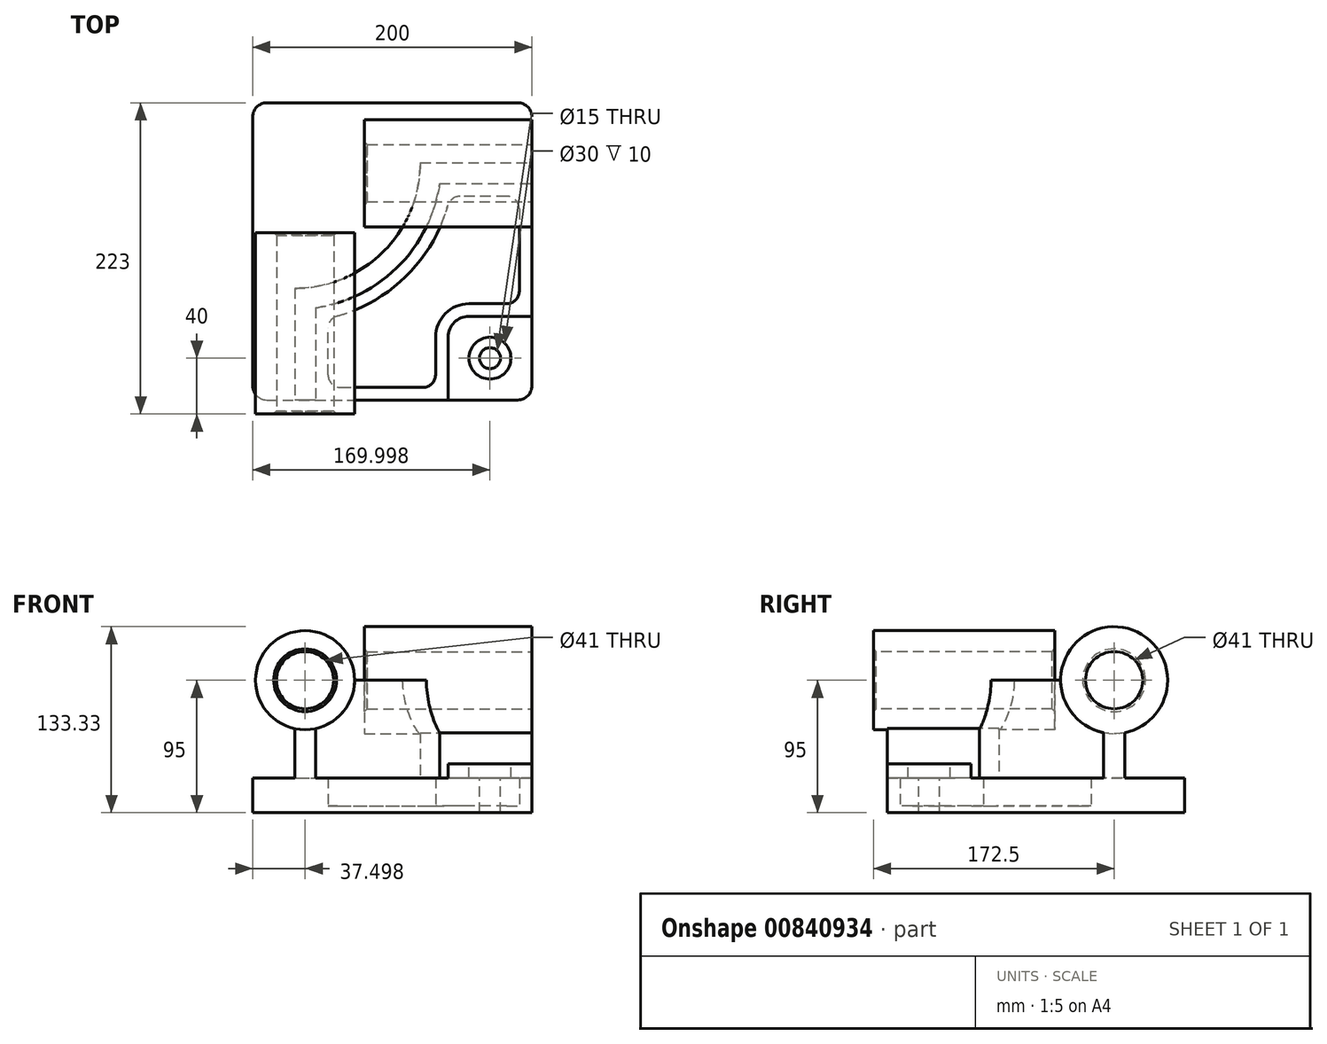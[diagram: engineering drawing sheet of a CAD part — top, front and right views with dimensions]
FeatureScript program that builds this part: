
annotation { "Feature Type Name" : "Feature", "Feature Type Description" : "" }
export const myFeature = defineFeature(function(context is Context, id is Id, definition is map)
    precondition{}
    {
        {
            assignVariable(context, id + "F0", {"name" : "D", "anyValue" : 130});
        }
        {
            var Q0;
            Q0=qCreatedBy(makeId("Top.planeOp"),FACE);
            var sketch = newSketch(context, id + "F1", { "sketchPlane" : qUnion([Q0])});
            skLineSegment(sketch, "E0.bottom", {"start": v(-118.1, 102.93) * mm, "end": v(61.9, 102.93) * mm});
            skLineSegment(sketch, "E0.top", {"start": v(-118.1, -110.07) * mm, "end": v(-83.1, -110.07) * mm});
            skLineSegment(sketch, "E0.left", {"start": v(-128.1, 92.93) * mm, "end": v(-128.1, -100.07) * mm});
            skLineSegment(sketch, "E0.right", {"start": v(71.9, 92.93) * mm, "end": v(71.9, 44.93) * mm});
            skCircle(sketch, "E1", {"center": v(41.9, -80.07) * mm, "radius": 11.73 * mm});
            skCircle(sketch, "E2", {"center": v(41.9, -80.07) * mm, "radius": 6.14 * mm});
            skPoint(sketch, "E3.visualSharp", {"position": v(-128.1, 102.93) * mm});
            skArc(sketch, "E3.filletArc", {"start": v(-118.1, 102.93) * mm, "mid": v(-125.16, 100) * mm, "end": v(-128.1, 92.93) * mm});
            skPoint(sketch, "E4.visualSharp", {"position": v(-128.1, -110.07) * mm});
            skArc(sketch, "E4.filletArc", {"start": v(-128.1, -100.07) * mm, "mid": v(-125.16, -107.14) * mm, "end": v(-118.1, -110.07) * mm});
            skPoint(sketch, "E5.visualSharp", {"position": v(71.9, -110.07) * mm});
            skArc(sketch, "E5.filletArc", {"start": v(61.9, -110.07) * mm, "mid": v(68.98, -107.14) * mm, "end": v(71.9, -100.07) * mm});
            skPoint(sketch, "E6.visualSharp", {"position": v(71.9, 102.93) * mm});
            skArc(sketch, "E6.filletArc", {"start": v(71.9, 92.93) * mm, "mid": v(68.98, 100) * mm, "end": v(61.9, 102.93) * mm});
            skLineSegment(sketch, "E7", {"start": v(71.9, -50.07) * mm, "end": v(26.9, -50.07) * mm});
            skLineSegment(sketch, "E8", {"start": v(11.9, -65.07) * mm, "end": v(11.9, -110.07) * mm});
            skPoint(sketch, "E9", {"position": v(41.9, -50.07) * mm});
            skPoint(sketch, "E10", {"position": v(11.9, -80.07) * mm});
            skPoint(sketch, "E11.visualSharp", {"position": v(11.9, -50.07) * mm});
            skArc(sketch, "E11.filletArc", {"start": v(26.9, -50.07) * mm, "mid": v(16.3, -54.46) * mm, "end": v(11.9, -65.07) * mm});
            skLineSegment(sketch, "E12", {"start": v(-98.1, -110.07) * mm, "end": v(-98.1, -30.07) * mm});
            skLineSegment(sketch, "E13", {"start": v(71.9, 59.93) * mm, "end": v(-8.1, 59.93) * mm});
            skArc(sketch, "E14", {"start": v(-98.1, -30.07) * mm, "mid": v(-34.45, -3.7) * mm, "end": v(-8.1, 59.93) * mm});
            skLineSegment(sketch, "E15.0", {"start": v(71.9, 44.93) * mm, "end": v(5.83, 44.93) * mm});
            skArc(sketch, "E15.1", {"start": v(-83.1, -44) * mm, "mid": v(-23.85, -14.32) * mm, "end": v(5.83, 44.93) * mm});
            skLineSegment(sketch, "E15.2", {"start": v(-83.1, -110.07) * mm, "end": v(-83.1, -44) * mm});
            skLineSegment(sketch, "E16", {"start": v(71.9, 44.93) * mm, "end": v(71.9, -50.07) * mm});
            skLineSegment(sketch, "E17", {"start": v(71.9, -50.07) * mm, "end": v(71.9, -100.07) * mm});
            skLineSegment(sketch, "E18", {"start": v(11.9, -110.07) * mm, "end": v(61.9, -110.07) * mm});
            skLineSegment(sketch, "E19", {"start": v(-83.1, -110.07) * mm, "end": v(11.9, -110.07) * mm});
            skLineSegment(sketch, "E20.0", {"start": v(62.9, 26.93) * mm, "end": v(62.9, -32.07) * mm});
            skLineSegment(sketch, "E20.1", {"start": v(53.9, -41.07) * mm, "end": v(26.9, -41.07) * mm});
            skLineSegment(sketch, "E20.2", {"start": v(53.9, 35.93) * mm, "end": v(20.4, 35.93) * mm});
            skArc(sketch, "E20.3", {"start": v(26.9, -41.07) * mm, "mid": v(9.94, -48.1) * mm, "end": v(2.9, -65.07) * mm});
            skArc(sketch, "E20.4", {"start": v(-67.5, -49.9) * mm, "mid": v(-17.48, -20.68) * mm, "end": v(11.73, 29.34) * mm});
            skLineSegment(sketch, "E20.5", {"start": v(-74.1, -92.07) * mm, "end": v(-74.1, -58.56) * mm});
            skLineSegment(sketch, "E20.6", {"start": v(-65.1, -101.07) * mm, "end": v(-6.1, -101.07) * mm});
            skLineSegment(sketch, "E20.7", {"start": v(2.9, -65.07) * mm, "end": v(2.9, -92.07) * mm});
            skPoint(sketch, "E21.visualSharp", {"position": v(2.9, -101.07) * mm});
            skArc(sketch, "E21.filletArc", {"start": v(-6.1, -101.07) * mm, "mid": v(0.27, -98.43) * mm, "end": v(2.9, -92.07) * mm});
            skPoint(sketch, "E22.visualSharp", {"position": v(-74.1, -101.07) * mm});
            skArc(sketch, "E22.filletArc", {"start": v(-74.1, -92.07) * mm, "mid": v(-71.46, -98.43) * mm, "end": v(-65.1, -101.07) * mm});
            skPoint(sketch, "E23.visualSharp", {"position": v(-74.1, -51.51) * mm});
            skArc(sketch, "E23.filletArc", {"start": v(-67.5, -49.9) * mm, "mid": v(-72.26, -53.12) * mm, "end": v(-74.1, -58.56) * mm});
            skPoint(sketch, "E24.visualSharp", {"position": v(13.35, 35.93) * mm});
            skArc(sketch, "E24.filletArc", {"start": v(20.4, 35.93) * mm, "mid": v(14.95, 34.1) * mm, "end": v(11.73, 29.34) * mm});
            skPoint(sketch, "E25.visualSharp", {"position": v(62.9, 35.93) * mm});
            skArc(sketch, "E25.filletArc", {"start": v(62.9, 26.93) * mm, "mid": v(60.27, 33.3) * mm, "end": v(53.9, 35.93) * mm});
            skPoint(sketch, "E26.visualSharp", {"position": v(62.9, -41.07) * mm});
            skArc(sketch, "E26.filletArc", {"start": v(53.9, -41.07) * mm, "mid": v(60.27, -38.43) * mm, "end": v(62.9, -32.07) * mm});
            skSolve(sketch);
        }
        {
            var Q0;
            Q0=makeQuery(id+"F1.imprint","IMPRINT",FACE,{"disambiguationData":[TD([[makeQuery(id+"F1.imprint","IMPRINT",EDGE,{"derivedFrom":sQuery(id+"F1.wireOp",EDGE,"E20.0")}),-1.0]])]});
            var Q1;
            Q1=makeQuery(id+"F1.imprint","IMPRINT",FACE,{"disambiguationData":[TD([[makeQuery(id+"F1.imprint","IMPRINT",EDGE,{"derivedFrom":sQuery(id+"F1.wireOp",EDGE,"E7")}),-1.0]])]});
            var Q2;
            {var subQ3=sQuery(id+"F1.wireOp",EDGE,"E12");Q2=makeQuery(id+"F1.imprint","IMPRINT",FACE,{"disambiguationData":[TD([[makeQuery(id+"F1.imprint","IMPRINT",EDGE,{"derivedFrom":subQ3}),-1.0]])]});}
            var Q3;
            Q3=makeQuery(id+"F1.imprint","IMPRINT",FACE,{"disambiguationData":[TD([[makeQuery(id+"F1.imprint","IMPRINT",EDGE,{"derivedFrom":sQuery(id+"F1.wireOp",EDGE,"E0.bottom")}),-1.0]])]});
            var Q4;
            Q4=makeQuery(id+"F1.imprint","IMPRINT",FACE,{"disambiguationData":[TD([[makeQuery(id+"F1.imprint","IMPRINT",EDGE,{"derivedFrom":sQuery(id+"F1.wireOp",EDGE,"E1")}),-1.0]])]});
            var Q5;
            Q5=makeQuery(id+"F1.imprint","IMPRINT",FACE,{"disambiguationData":[TD([[makeQuery(id+"F1.imprint","IMPRINT",EDGE,{"derivedFrom":sQuery(id+"F1.wireOp",EDGE,"E2")}),1.0]])]});
            var Q6;
            Q6=makeQuery(id+"F1.imprint","IMPRINT",FACE,{"disambiguationData":[TD([[makeQuery(id+"F1.imprint","IMPRINT",EDGE,{"derivedFrom":sQuery(id+"F1.wireOp",EDGE,"E1")}),1.0]])]});
            extrude(context, id + "F2", {"entities" : qUnion([Q0, Q1, Q2, Q3, Q4, Q5, Q6]), "depth" : 25 * mm, "offsetDistance" : 25 * mm});
        }
        {
            var Q0;
            Q0=makeQuery(id+"F1.imprint","IMPRINT",FACE,{"disambiguationData":[TD([[makeQuery(id+"F1.imprint","IMPRINT",EDGE,{"derivedFrom":sQuery(id+"F1.wireOp",EDGE,"E2")}),1.0]])]});
            var Q1;
            Q1=makeQuery(id+"F1.imprint","IMPRINT",FACE,{"disambiguationData":[TD([[makeQuery(id+"F1.imprint","IMPRINT",EDGE,{"derivedFrom":sQuery(id+"F1.wireOp",EDGE,"E1")}),1.0]])]});
            var Q2;
            Q2=makeQuery(id+"F1.imprint","IMPRINT",FACE,{"disambiguationData":[TD([[makeQuery(id+"F1.imprint","IMPRINT",EDGE,{"derivedFrom":sQuery(id+"F1.wireOp",EDGE,"E1")}),-1.0]])]});
            extrude(context, id + "F3", {"entities" : qUnion([Q0, Q1, Q2]), "operationType" : NewBodyOperationType.ADD, "depth" : 35 * mm, "offsetDistance" : 25 * mm});
        }
        {
            var Q0;
            {var subQ0=sQuery(id+"F1.wireOp",EDGE,"E18");Q0=makeQuery(id+"F3.boolean.opBoolean","MERGE",FACE,{"derivedFrom":[makeQuery(id+"F2.opExtrude","SWEPT_FACE",FACE,{"disambiguationData":[OSD([sQuery(id+"F1.wireOp",EDGE,"E0.top"),subQ0,sQuery(id+"F1.wireOp",EDGE,"E19")])]}),makeQuery(id+"F3.opExtrude","SWEPT_FACE",FACE,{"disambiguationData":[OSD([subQ0])]})]});}
            var sketch = newSketch(context, id + "F4", { "sketchPlane" : qUnion([Q0])});
            skLineSegment(sketch, "E27", {"start": v(-98.1, 0) * mm, "end": v(-98.1, 60.3) * mm});
            skLineSegment(sketch, "E28", {"start": v(-83.1, 0) * mm, "end": v(-83.1, 60.3) * mm});
            skCircle(sketch, "E29", {"center": v(-90.6, 95) * mm, "radius": 35.5 * mm});
            skCircle(sketch, "E30", {"center": v(-90.6, 95) * mm, "radius": 20.5 * mm});
            skSolve(sketch);
        }
        {
            var Q0;
            {var subQ3=sQuery(id+"F1.wireOp",EDGE,"E12");Q0=makeQuery(id+"F1.imprint","IMPRINT",FACE,{"disambiguationData":[TD([[makeQuery(id+"F1.imprint","IMPRINT",EDGE,{"derivedFrom":subQ3}),-1.0]])]});}
            extrude(context, id + "F5", {"entities" : qUnion([Q0]), "operationType" : NewBodyOperationType.ADD, "depth" : 95 * mm, "offsetDistance" : 25 * mm});
        }
        {
            var Q0;
            Q0=makeQuery(id+"F4.imprint","IMPRINT",FACE,{"disambiguationData":[TD([[makeQuery(id+"F4.imprint","IMPRINT",EDGE,{"derivedFrom":sQuery(id+"F4.wireOp",EDGE,"E30")}),-1.0]])]});
            extrude(context, id + "F6", {"entities" : qUnion([Q0]), "operationType" : NewBodyOperationType.ADD, "oppositeDirection" : true, "depth" : (getVariable(context, 'D') - 10) * mm, "offsetDistance" : 25 * mm, "hasSecondDirection" : true, "secondDirectionOppositeDirection" : false, "secondDirectionDepth" : 10 * mm});
        }
        {
            var Q0;
            Q0=makeQuery(id+"F4.imprint","IMPRINT",FACE,{"disambiguationData":[TD([[makeQuery(id+"F4.imprint","IMPRINT",EDGE,{"derivedFrom":sQuery(id+"F4.wireOp",EDGE,"E30")}),1.0]])]});
            extrude(context, id + "F7", {"entities" : qUnion([Q0]), "operationType" : NewBodyOperationType.REMOVE, "endBound" : BoundingType.THROUGH_ALL, "oppositeDirection" : true, "depth" : 25 * mm, "offsetDistance" : 25 * mm});
        }
        {
            var Q0;
            Q0=makeQuery(id+"F1.imprint","IMPRINT",FACE,{"disambiguationData":[TD([[makeQuery(id+"F1.imprint","IMPRINT",EDGE,{"derivedFrom":sQuery(id+"F1.wireOp",EDGE,"E20.0")}),-1.0]])]});
            var Q1;
            {var subQ0=sQuery(id+"F1.wireOp",EDGE,"E0.right");var subQ1=sQuery(id+"F1.wireOp",EDGE,"E18");var subQ2=sQuery(id+"F1.wireOp",EDGE,"E17");var subQ3=sQuery(id+"F1.wireOp",EDGE,"E0.top");var subQ4=sQuery(id+"F1.wireOp",EDGE,"E19");var subQ5=sQuery(id+"F1.wireOp",EDGE,"E16");Q1=makeQuery(id+"F5.boolean.opBoolean","SPLIT",FACE,{"disambiguationData":[TD([makeQuery(id+"F3.opExtrude","SWEPT_FACE",FACE,{"disambiguationData":[OSD([sQuery(id+"F1.wireOp",EDGE,"E7")])]})])],"derivedFrom":makeQuery(id+"F2.opExtrude","CAP_FACE",FACE,{"disambiguationData":[OSD([sQuery(id+"F1.wireOp",EDGE,"E0.bottom"),subQ3,sQuery(id+"F1.wireOp",EDGE,"E0.left"),subQ0,sQuery(id+"F1.wireOp",EDGE,"E3.filletArc"),sQuery(id+"F1.wireOp",EDGE,"E4.filletArc"),sQuery(id+"F1.wireOp",EDGE,"E5.filletArc"),sQuery(id+"F1.wireOp",EDGE,"E6.filletArc"),subQ5,subQ2,subQ1,subQ4])],"isStart":false})});}
            extrude(context, id + "F8", {"entities" : qUnion([Q0]), "operationType" : NewBodyOperationType.REMOVE, "endBound" : BoundingType.UP_TO_SURFACE, "depth" : 25 * mm, "endBoundEntityFace" : qUnion([Q1]), "offsetDistance" : 25 * mm, "hasSecondDirection" : true, "secondDirectionOppositeDirection" : false, "secondDirectionDepth" : 5 * mm});
        }
        {
            var Q0;
            {var subQ0=sQuery(id+"F1.wireOp",EDGE,"E0.right");var subQ1=sQuery(id+"F1.wireOp",EDGE,"E17");Q0=makeQuery(id+"F5.boolean.opBoolean","MERGE",FACE,{"derivedFrom":[makeQuery(id+"F3.boolean.opBoolean","MERGE",FACE,{"derivedFrom":[makeQuery(id+"F2.opExtrude","SWEPT_FACE",FACE,{"disambiguationData":[OSD([subQ0,sQuery(id+"F1.wireOp",EDGE,"E16"),subQ1])]}),makeQuery(id+"F3.opExtrude","SWEPT_FACE",FACE,{"disambiguationData":[OSD([subQ1])]})]}),makeQuery(id+"F5.opExtrude","SWEPT_FACE",FACE,{"disambiguationData":[OSD([subQ0])]})]});}
            var sketch = newSketch(context, id + "F9", { "sketchPlane" : qUnion([Q0])});
            skCircle(sketch, "E31", {"center": v(52.43, 95) * mm, "radius": 38.33 * mm});
            skPoint(sketch, "E31.centerSnap0", {"position": v(52.43, 95) * mm});
            skCircle(sketch, "E32", {"center": v(52.43, 95) * mm, "radius": 20.5 * mm});
            skSolve(sketch);
        }
        {
            var Q0;
            {var subQ0=sQuery(id+"F9.wireOp",EDGE,"E31");var subQ1=sQuery(id+"F1.wireOp",EDGE,"E0.right");var subQ4=makeQuery(id+"F5.opExtrude","SWEPT_EDGE",EDGE,{"disambiguationData":[OSD([subQ1,sQuery(id+"F1.wireOp",EDGE,"E13")])]});var subQ5=makeQuery(id+"F9.imprint","INTERSECT",VERTEX,{"derivedFrom":[subQ4,subQ0]});Q0=makeQuery(id+"F9.imprint","IMPRINT",FACE,{"disambiguationData":[TD([[makeQuery(id+"F9.imprint","IMPRINT",EDGE,{"disambiguationData":[TD([[subQ5,-1.0]])],"derivedFrom":subQ0}),1.0]])]});}
            var Q1;
            {var subQ0=sQuery(id+"F9.wireOp",EDGE,"E31");var subQ1=sQuery(id+"F1.wireOp",EDGE,"E0.right");var subQ4=makeQuery(id+"F5.opExtrude","SWEPT_EDGE",EDGE,{"disambiguationData":[OSD([subQ1,sQuery(id+"F1.wireOp",EDGE,"E13")])]});var subQ5=makeQuery(id+"F9.imprint","INTERSECT",VERTEX,{"derivedFrom":[subQ4,subQ0]});Q1=makeQuery(id+"F9.imprint","IMPRINT",FACE,{"disambiguationData":[TD([[makeQuery(id+"F9.imprint","IMPRINT",EDGE,{"disambiguationData":[TD([[subQ5,1.0]])],"derivedFrom":subQ0}),1.0]])]});}
            extrude(context, id + "F10", {"entities" : qUnion([Q0, Q1]), "operationType" : NewBodyOperationType.ADD, "oppositeDirection" : true, "depth" : (getVariable(context, 'D') - 10) * mm, "offsetDistance" : 25 * mm});
        }
        {
            var Q0;
            {var subQ1=sQuery(id+"F1.wireOp",EDGE,"E0.right");var subQ6=makeQuery(id+"F5.opExtrude","CAP_EDGE",EDGE,{"disambiguationData":[OSD([subQ1])],"isStart":false});Q0=makeQuery(id+"F9.imprint","IMPRINT",FACE,{"disambiguationData":[TD([[makeQuery(id+"F9.imprint","IMPRINT",EDGE,{"derivedFrom":subQ6}),1.0]])]});}
            var Q1;
            {var subQ1=sQuery(id+"F1.wireOp",EDGE,"E0.right");var subQ6=makeQuery(id+"F5.opExtrude","CAP_EDGE",EDGE,{"disambiguationData":[OSD([subQ1])],"isStart":false});Q1=makeQuery(id+"F9.imprint","IMPRINT",FACE,{"disambiguationData":[TD([[makeQuery(id+"F9.imprint","IMPRINT",EDGE,{"derivedFrom":subQ6}),-1.0]])]});}
            extrude(context, id + "F11", {"entities" : qUnion([Q0, Q1]), "operationType" : NewBodyOperationType.REMOVE, "endBound" : BoundingType.THROUGH_ALL, "oppositeDirection" : true, "depth" : 25 * mm, "offsetDistance" : 25 * mm});
        }
        {
            var Q0;
            Q0=makeQuery(id+"F6.opExtrude","CAP_EDGE",EDGE,{"disambiguationData":[OSD([sQuery(id+"F4.wireOp",EDGE,"E30")])],"isStart":true});
            var Q1;
            Q1=makeQuery(id+"F6.opExtrude","CAP_EDGE",EDGE,{"disambiguationData":[OSD([sQuery(id+"F4.wireOp",EDGE,"E30")])],"isStart":false});
            var Q2;
            Q2=makeQuery(id+"F10.opExtrude","CAP_EDGE",EDGE,{"disambiguationData":[OSD([sQuery(id+"F9.wireOp",EDGE,"E32")])],"isStart":false});
            var Q3;
            {var subQ0=sQuery(id+"F9.wireOp",EDGE,"E32");Q3=makeQuery(id+"F11.boolean.opBoolean","MERGE",EDGE,{"derivedFrom":[makeQuery(id+"F10.opExtrude","CAP_EDGE",EDGE,{"disambiguationData":[OSD([subQ0])],"isStart":true}),makeQuery(id+"F11.opExtrude","CAP_EDGE",EDGE,{"disambiguationData":[OSD([subQ0])],"isStart":true})]});}
            chamfer(context, id + "F12", {"entities" : qUnion([Q0, Q1, Q2, Q3]), "chamferType" : ChamferType.OFFSET_ANGLE, "width" : 2 * mm, "oppositeDirection" : false, "angle" : 45 * degree, "tangentPropagation" : true});
        }
        {
            var Q0;
            Q0=makeQuery(id+"F3.opExtrude","CAP_FACE",FACE,{"disambiguationData":[OSD([sQuery(id+"F1.wireOp",EDGE,"E5.filletArc"),sQuery(id+"F1.wireOp",EDGE,"E7"),sQuery(id+"F1.wireOp",EDGE,"E8"),sQuery(id+"F1.wireOp",EDGE,"E11.filletArc"),sQuery(id+"F1.wireOp",EDGE,"E17"),sQuery(id+"F1.wireOp",EDGE,"E18")])],"isStart":false});
            var sketch = newSketch(context, id + "F13", { "sketchPlane" : qUnion([Q0])});
            skPoint(sketch, "E33.0", {"position": v(41.9, -80.07) * mm});
            skSolve(sketch);
        }
        {
            var Q0;
            Q0=sQuery(id+"F13.wireOp",VERTEX,"E33.0");
            var Q1;
            Q1=makeQuery(id+"F2.opExtrude","SWEPT_BODY",BODY,{"disambiguationData":[OSD([sQuery(id+"F1.wireOp",EDGE,"E0.bottom"),sQuery(id+"F1.wireOp",EDGE,"E0.top"),sQuery(id+"F1.wireOp",EDGE,"E0.left"),sQuery(id+"F1.wireOp",EDGE,"E0.right"),sQuery(id+"F1.wireOp",EDGE,"E3.filletArc"),sQuery(id+"F1.wireOp",EDGE,"E4.filletArc"),sQuery(id+"F1.wireOp",EDGE,"E5.filletArc"),sQuery(id+"F1.wireOp",EDGE,"E6.filletArc"),sQuery(id+"F1.wireOp",EDGE,"E16"),sQuery(id+"F1.wireOp",EDGE,"E17"),sQuery(id+"F1.wireOp",EDGE,"E18"),sQuery(id+"F1.wireOp",EDGE,"E19")])]});
            hole(context, id + "F14", {"style" : HoleStyle.C_BORE, "endStyle" : HoleEndStyle.THROUGH, "holeDiameter" : 15 * mm, "cBoreDiameter" : 30 * mm, "cBoreDepth" : 10 * mm, "majorDiameter" : 6.35 * mm, "isTappedThrough" : true, "tappedDepth" : 16 * mm, "tapClearance" : 3, "startFromSketch" : true, "locations" : qUnion([Q0]), "scope" : qUnion([Q1])});
        }
    });
